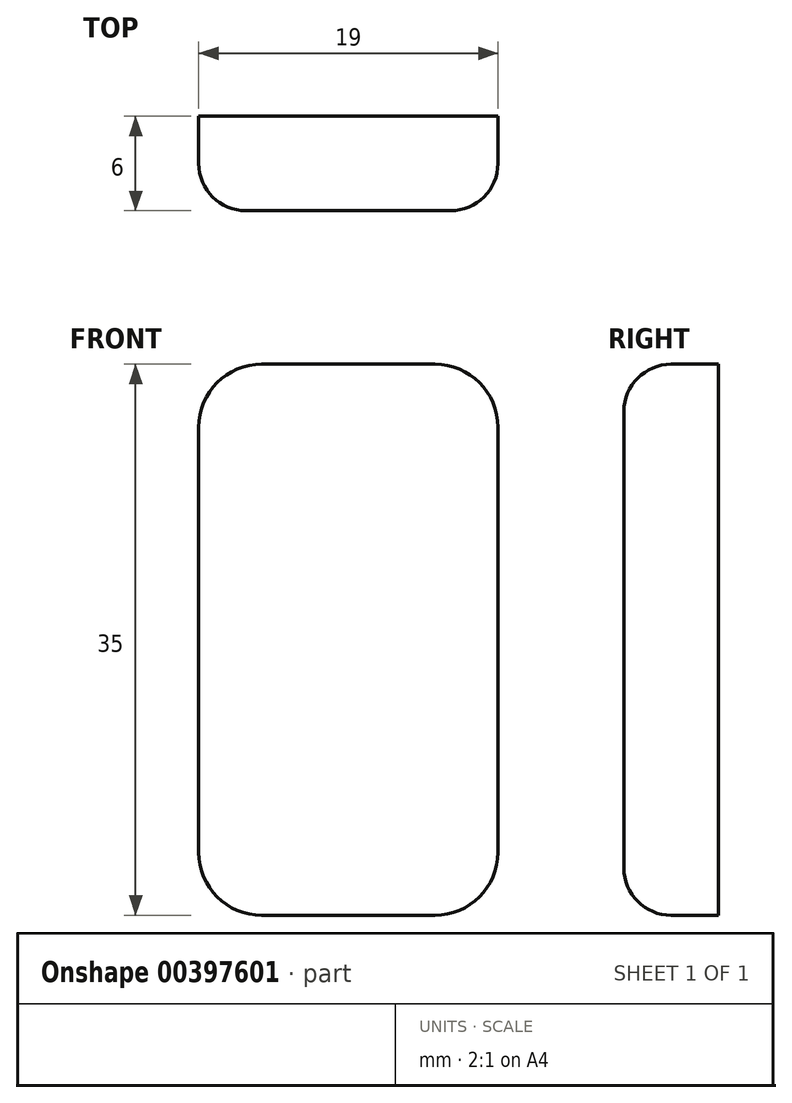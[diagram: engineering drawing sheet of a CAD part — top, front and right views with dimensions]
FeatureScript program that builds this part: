
annotation { "Feature Type Name" : "Feature", "Feature Type Description" : "" }
export const myFeature = defineFeature(function(context is Context, id is Id, definition is map)
    precondition{}
    {
        {
            var Q0;
            Q0=qCreatedBy(makeId("Front.planeOp"),FACE);
            var sketch = newSketch(context, id + "F0", { "sketchPlane" : qUnion([Q0])});
            skLineSegment(sketch, "E0.bottom", {"start": v(4.96, -0.18) * mm, "end": v(-14.04, -0.18) * mm});
            skLineSegment(sketch, "E0.top", {"start": v(4.96, 34.82) * mm, "end": v(-14.04, 34.82) * mm});
            skLineSegment(sketch, "E0.left", {"start": v(4.96, -0.18) * mm, "end": v(4.96, 34.82) * mm});
            skLineSegment(sketch, "E0.right", {"start": v(-14.04, -0.18) * mm, "end": v(-14.04, 34.82) * mm});
            skPoint(sketch, "E0.middle", {"position": v(-4.54, 17.32) * mm});
            skSolve(sketch);
        }
        {
            var Q0;
            Q0=qSketchRegion(id+"F0",true);
            extrude(context, id + "F1", {"entities" : qUnion([Q0]), "depth" : 6 * mm});
        }
        {
            var Q0;
            Q0=makeQuery(id+"F1.opExtrude","SWEPT_EDGE",EDGE,{"disambiguationData":[OSD([sQuery(id+"F0.wireOp",EDGE,"E0.top"),sQuery(id+"F0.wireOp",EDGE,"E0.left")])]});
            var Q1;
            Q1=makeQuery(id+"F1.opExtrude","SWEPT_EDGE",EDGE,{"disambiguationData":[OSD([sQuery(id+"F0.wireOp",EDGE,"E0.bottom"),sQuery(id+"F0.wireOp",EDGE,"E0.left")])]});
            var Q2;
            Q2=makeQuery(id+"F1.opExtrude","SWEPT_EDGE",EDGE,{"disambiguationData":[OSD([sQuery(id+"F0.wireOp",EDGE,"E0.top"),sQuery(id+"F0.wireOp",EDGE,"E0.right")])]});
            var Q3;
            Q3=makeQuery(id+"F1.opExtrude","SWEPT_EDGE",EDGE,{"disambiguationData":[OSD([sQuery(id+"F0.wireOp",EDGE,"E0.bottom"),sQuery(id+"F0.wireOp",EDGE,"E0.right")])]});
            fillet(context, id + "F2", {"entities" : qUnion([Q0, Q1, Q2, Q3]), "radius" : 4 * mm, "tangentPropagation" : true, "allowEdgeOverflow" : false});
        }
        {
            var Q0;
            Q0=makeQuery(id+"F1.opExtrude","CAP_EDGE",EDGE,{"disambiguationData":[OSD([sQuery(id+"F0.wireOp",EDGE,"E0.right")])],"isStart":false});
            fillet(context, id + "F3", {"entities" : qUnion([Q0]), "radius" : 3 * mm, "tangentPropagation" : true, "allowEdgeOverflow" : false});
        }
    });
